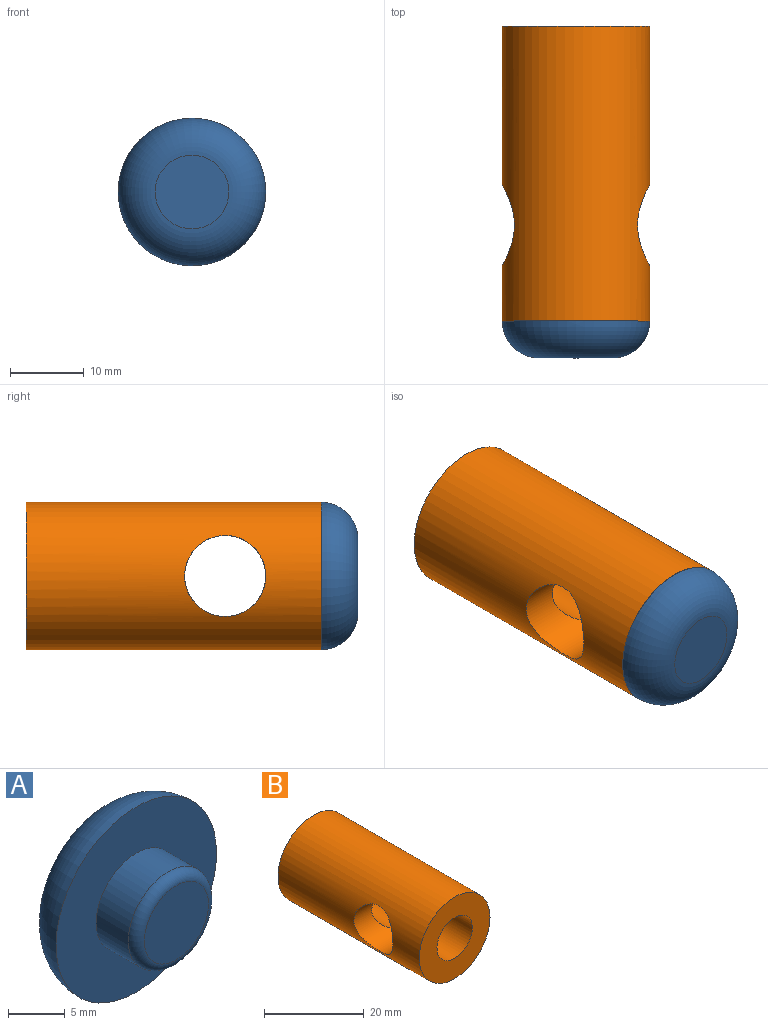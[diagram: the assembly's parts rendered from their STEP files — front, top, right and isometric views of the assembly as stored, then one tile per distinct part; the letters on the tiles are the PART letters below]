
ASSEMBLY  parts=2 mates=1
PART A: 6 faces, bbox 21.6x10x21.6 mm
  f0: plane 10x10mm, normal (0,1,0), area 78.5mm2, adj f4
  f1: cylinder r=5mm len=10mm, axis (0,-1,0), area 125.7mm2, adj f2,f5
  f2: plane 20x20mm, normal (0,-1,0), area 235.6mm2, adj f1,f4
  f3: plane 8x8mm, normal (0,-1,0), area 50.3mm2, adj f5
  f4: torus R=5mm, axis (0,-1,0), area 403.8mm2, adj f0,f2
  f5: torus R=4mm, axis (0,-1,0), area 45.8mm2, adj f1,f3
PART B: 8 faces, bbox 20x40x20 mm
  f0: cylinder r=5mm len=19.71mm, axis (0,-1,0), area 563.5mm2, adj f5,f7
  f1: cylinder r=2.25mm len=5mm, axis (0,1,0), area 70.7mm2, adj f4,f5
  f2: cylinder r=10mm len=40mm, axis (0,1,0), area 2315.2mm2, adj f3,f4,f7
  f3: plane 20x20mm, normal (0,-1,0), area 235.6mm2, adj f2,f6
  f4: plane 20x20mm, normal (0,1,0), area 298.3mm2, adj f1,f2
  f5: plane 10x10mm, normal (0,-1,0), area 62.6mm2, adj f0,f1
  f6: cylinder r=5mm len=10.71mm, axis (0,-1,0), area 280.8mm2, adj f3,f7
  f7: cylinder r=5.5mm len=20mm, axis (1,0,0), area 452.3mm2, adj f0,f2,f6
PLACE A rot(axis=(1,0,0),180deg) t=(-21.36,-52.35,3.88)mm
PLACE B t=(-21.36,-7.35,3.88)mm
MATE parallel B.f0 <-> A.f1  axis (0,-1,0) through (-21.36,-47.35,3.88)mm
